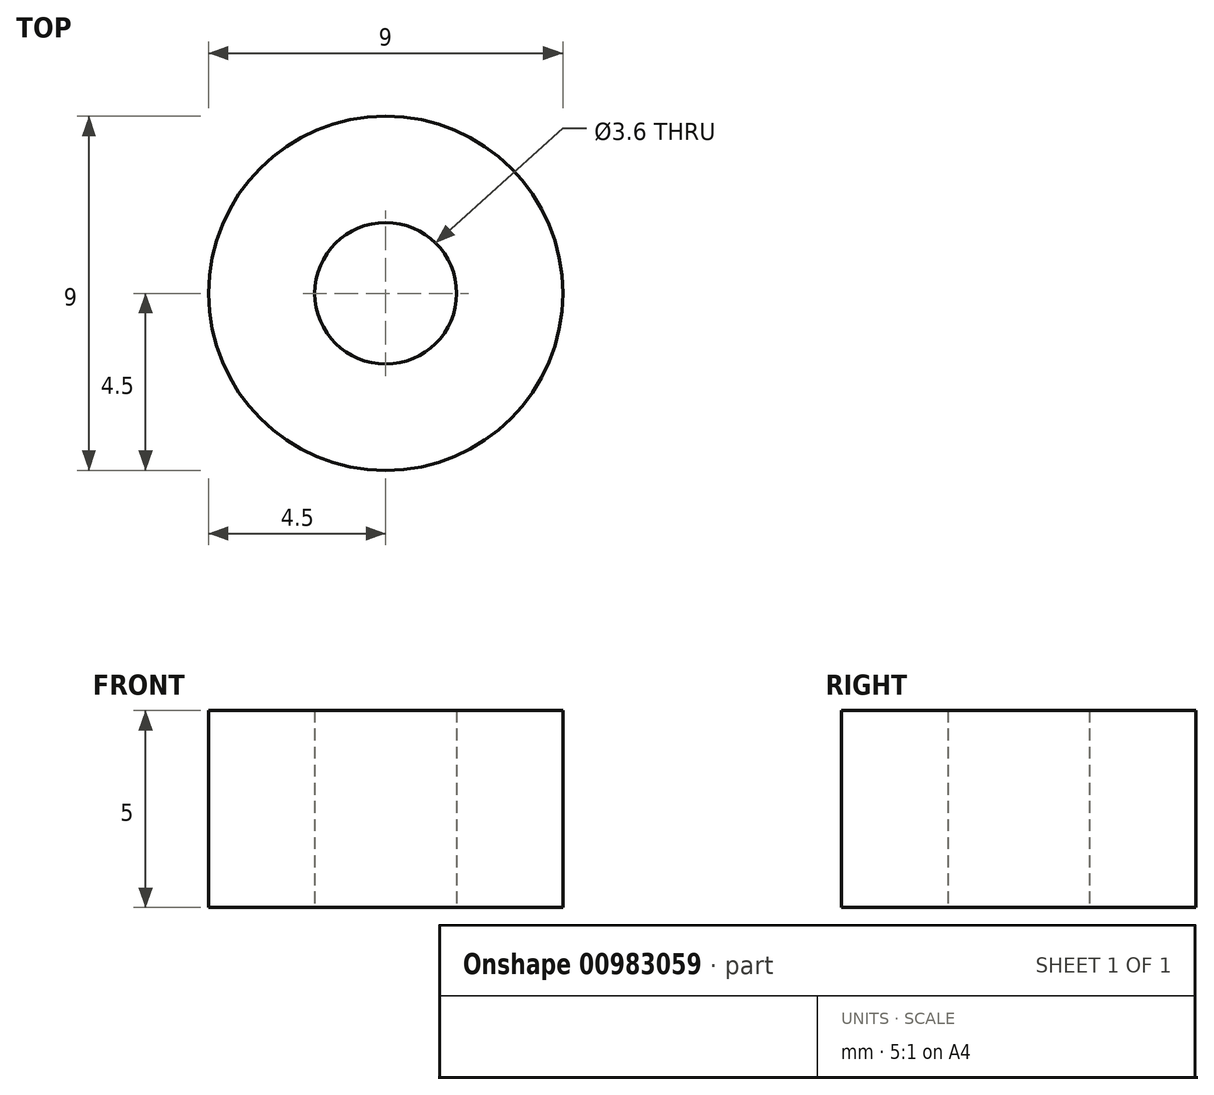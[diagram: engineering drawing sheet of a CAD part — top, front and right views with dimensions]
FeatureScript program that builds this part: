
annotation { "Feature Type Name" : "Feature", "Feature Type Description" : "" }
export const myFeature = defineFeature(function(context is Context, id is Id, definition is map)
    precondition{}
    {
        {
            var Q0;
            Q0=qCreatedBy(makeId("Top.planeOp"),FACE);
            var sketch = newSketch(context, id + "F0", { "sketchPlane" : qUnion([Q0])});
            skCircle(sketch, "E0", {"center": v(0, 0) * mm, "radius": 1.8 * mm});
            skCircle(sketch, "E1", {"center": v(0, 0) * mm, "radius": 4.5 * mm});
            skSolve(sketch);
        }
        {
            var Q0;
            Q0=makeQuery(id+"F0.imprint","IMPRINT",FACE,{"disambiguationData":[TD([[makeQuery(id+"F0.imprint","IMPRINT",EDGE,{"derivedFrom":sQuery(id+"F0.wireOp",EDGE,"E0")}),-1.0]])]});
            extrude(context, id + "F1", {"entities" : qUnion([Q0]), "depth" : 5 * mm, "offsetDistance" : 25 * mm});
        }
    });
